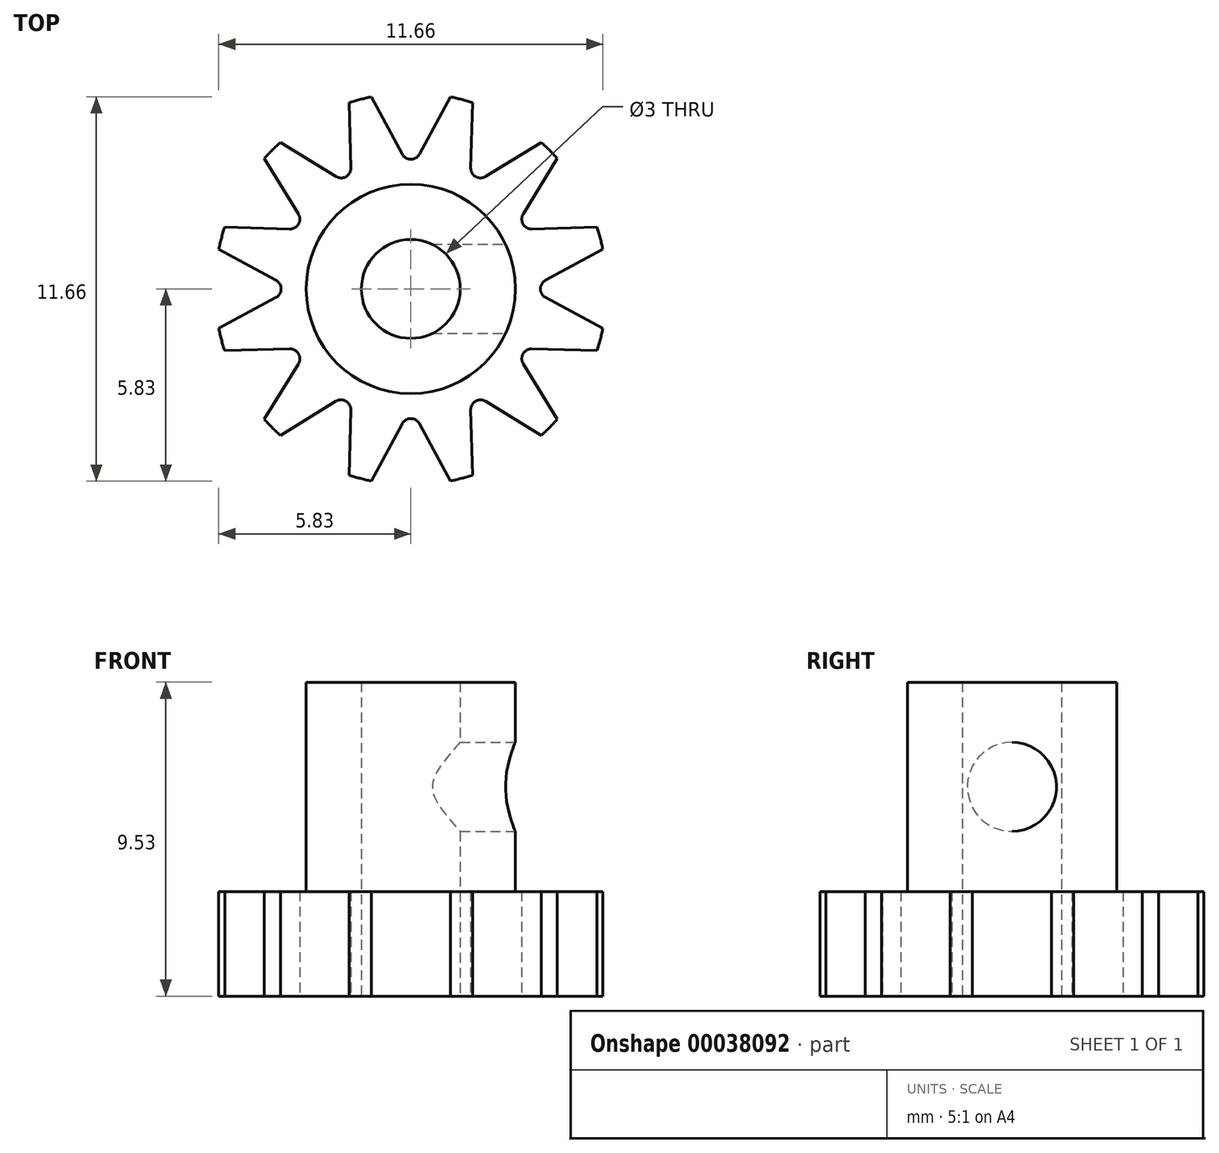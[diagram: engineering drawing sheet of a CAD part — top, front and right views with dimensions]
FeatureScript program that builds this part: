
annotation { "Feature Type Name" : "Feature", "Feature Type Description" : "" }
export const myFeature = defineFeature(function(context is Context, id is Id, definition is map)
    precondition{}
    {
        {
            var Q0;
            Q0=qCreatedBy(makeId("Top.planeOp"),FACE);
            var sketch = newSketch(context, id + "F0", { "sketchPlane" : qUnion([Q0])});
            skCircle(sketch, "E0", {"center": v(0, 0) * mm, "radius": 5.95 * mm});
            skCircle(sketch, "E1", {"center": v(0, 0) * mm, "radius": 1.5 * mm});
            skSolve(sketch);
        }
        {
            var Q0;
            Q0 = qSketchRegion(id + "F0", true);
            extrude(context, id + "F1", {"entities" : qUnion([Q0]), "depth" : 3.17 * mm});
        }
        {
            var Q0;
            Q0=makeQuery(id+"F1.opExtrude","CAP_FACE",FACE,{"disambiguationData":[OSD([sQuery(id+"F0.wireOp",EDGE,"E0"),sQuery(id+"F0.wireOp",EDGE,"E1")])],"isStart":false});
            var sketch = newSketch(context, id + "F2", { "sketchPlane" : qUnion([Q0])});
            skLineSegment(sketch, "E2.rect.bottom", {"start": v(3.18, -3.17) * mm, "end": v(-3.17, -3.17) * mm});
            skLineSegment(sketch, "E2.rect.top", {"start": v(3.17, 3.18) * mm, "end": v(-3.18, 3.17) * mm});
            skLineSegment(sketch, "E2.rect.left", {"start": v(3.18, -3.17) * mm, "end": v(3.17, 3.18) * mm});
            skLineSegment(sketch, "E2.rect.right", {"start": v(-3.17, -3.17) * mm, "end": v(-3.18, 3.17) * mm});
            skPoint(sketch, "E2.rect.middle", {"position": v(0, 0) * mm});
            skCircle(sketch, "E3", {"center": v(0, 0) * mm, "radius": 1.5 * mm});
            skSolve(sketch);
        }
        {
            var Q0;
            Q0 = qSketchRegion(id + "F2", true);
            extrude(context, id + "F3", {"entities" : qUnion([Q0]), "operationType" : NewBodyOperationType.ADD, "depth" : 6.35 * mm});
        }
        {
            var Q0;
            Q0=makeQuery(id+"F3.opExtrude","SWEPT_FACE",FACE,{"disambiguationData":[OSD([sQuery(id+"F2.wireOp",EDGE,"E2.rect.left")])]});
            var sketch = newSketch(context, id + "F4", { "sketchPlane" : qUnion([Q0])});
            skLineSegment(sketch, "E4", {"start": v(-3.17, 6.35) * mm, "end": v(3.17, 6.35) * mm, "construction": true});
            skCircle(sketch, "E5", {"center": v(0, 6.35) * mm, "radius": 1.35 * mm});
            skSolve(sketch);
        }
        {
            var Q0;
            Q0 = qSketchRegion(id + "F4", true);
            var Q1;
            Q1=makeQuery(id+"F3.boolean.opBoolean","MERGE",FACE,{"derivedFrom":[makeQuery(id+"F1.opExtrude","SWEPT_FACE",FACE,{"disambiguationData":[OSD([sQuery(id+"F0.wireOp",EDGE,"E1")])]}),makeQuery(id+"F3.opExtrude","SWEPT_FACE",FACE,{"disambiguationData":[OSD([sQuery(id+"F2.wireOp",EDGE,"E3")])]})]});
            extrude(context, id + "F5", {"entities" : qUnion([Q0]), "operationType" : NewBodyOperationType.REMOVE, "endBound" : BoundingType.UP_TO_SURFACE, "oppositeDirection" : true, "endBoundEntityFace" : qUnion([Q1]), "depth" : 25.4 * mm});
        }
        {
            var Q0;
            Q0=makeQuery(id+"F3.opExtrude","SWEPT_EDGE",EDGE,{"disambiguationData":[OSD([sQuery(id+"F2.wireOp",EDGE,"E2.rect.bottom"),sQuery(id+"F2.wireOp",EDGE,"E2.rect.left")])]});
            var Q1;
            Q1=makeQuery(id+"F3.opExtrude","SWEPT_EDGE",EDGE,{"disambiguationData":[OSD([sQuery(id+"F2.wireOp",EDGE,"E2.rect.bottom"),sQuery(id+"F2.wireOp",EDGE,"E2.rect.right")])]});
            var Q2;
            Q2=makeQuery(id+"F3.opExtrude","SWEPT_EDGE",EDGE,{"disambiguationData":[OSD([sQuery(id+"F2.wireOp",EDGE,"E2.rect.top"),sQuery(id+"F2.wireOp",EDGE,"E2.rect.left")])]});
            var Q3;
            Q3=makeQuery(id+"F3.opExtrude","SWEPT_EDGE",EDGE,{"disambiguationData":[OSD([sQuery(id+"F2.wireOp",EDGE,"E2.rect.top"),sQuery(id+"F2.wireOp",EDGE,"E2.rect.right")])]});
            fillet(context, id + "F6", {"entities" : qUnion([Q0, Q1, Q2, Q3]), "radius" : 3.17 * mm, "tangentPropagation" : true, "allowEdgeOverflow" : false});
        }
        {
            var Q0;
            Q0=makeQuery(id+"F1.opExtrude","CAP_FACE",FACE,{"disambiguationData":[OSD([sQuery(id+"F0.wireOp",EDGE,"E0"),sQuery(id+"F0.wireOp",EDGE,"E1")])],"isStart":true});
            var sketch = newSketch(context, id + "F7", { "sketchPlane" : qUnion([Q0])});
            skLineSegment(sketch, "E6", {"start": v(0, 0) * mm, "end": v(5.95, 0) * mm, "construction": true});
            skLineSegment(sketch, "E7", {"start": v(0, 0) * mm, "end": v(5.89, 0.87) * mm, "construction": true});
            skArc(sketch, "E8", {"start": v(5.83, -1.2) * mm, "mid": v(5.95, 0) * mm, "end": v(5.83, 1.2) * mm});
            skLineSegment(sketch, "E9", {"start": v(5.83, 1.2) * mm, "end": v(4.09, 0.26) * mm});
            skLineSegment(sketch, "E10", {"start": v(5.83, -1.2) * mm, "end": v(4.09, -0.26) * mm});
            skArc(sketch, "E11", {"start": v(4.09, 0.26) * mm, "mid": v(3.93, 0) * mm, "end": v(4.09, -0.26) * mm});
            skPoint(sketch, "E12", {"position": v(4.96, 0.73) * mm});
            skSolve(sketch);
        }
        {
            var Q0;
            Q0 = qSketchRegion(id + "F7", true);
            var Q1;
            Q1=makeQuery(id+"F1.opExtrude","CAP_FACE",FACE,{"disambiguationData":[OSD([sQuery(id+"F0.wireOp",EDGE,"E0"),sQuery(id+"F0.wireOp",EDGE,"E1")])],"isStart":false});
            extrude(context, id + "F8", {"entities" : qUnion([Q0]), "operationType" : NewBodyOperationType.REMOVE, "endBound" : BoundingType.UP_TO_SURFACE, "oppositeDirection" : true, "endBoundEntityFace" : qUnion([Q1]), "depth" : 25.4 * mm});
        }
        {
            var Q0;
            Q0=makeQuery(id+"F8.boolean.opBoolean","COPY",FACE,{"derivedFrom":makeQuery(id+"F8.opExtrude","SWEPT_FACE",FACE,{"disambiguationData":[OSD([sQuery(id+"F7.wireOp",EDGE,"E10")])]})});
            var Q1;
            Q1=makeQuery(id+"F8.boolean.opBoolean","COPY",FACE,{"derivedFrom":makeQuery(id+"F8.opExtrude","SWEPT_FACE",FACE,{"disambiguationData":[OSD([sQuery(id+"F7.wireOp",EDGE,"E11")])]})});
            var Q2;
            Q2=makeQuery(id+"F8.boolean.opBoolean","COPY",FACE,{"derivedFrom":makeQuery(id+"F8.opExtrude","SWEPT_FACE",FACE,{"disambiguationData":[OSD([sQuery(id+"F7.wireOp",EDGE,"E9")])]})});
            var Q3;
            Q3=makeQuery(id+"F1.opExtrude","SWEPT_FACE",FACE,{"disambiguationData":[OSD([sQuery(id+"F0.wireOp",EDGE,"E0")])]});
            circularPattern(context, id + "F9", {"faces" : qUnion([Q0, Q1, Q2]), "axis" : qUnion([Q3]), "angle" : 30 * degree, "instanceCount" : 12, "patternType" : PatternType.FACE});
        }
    });
